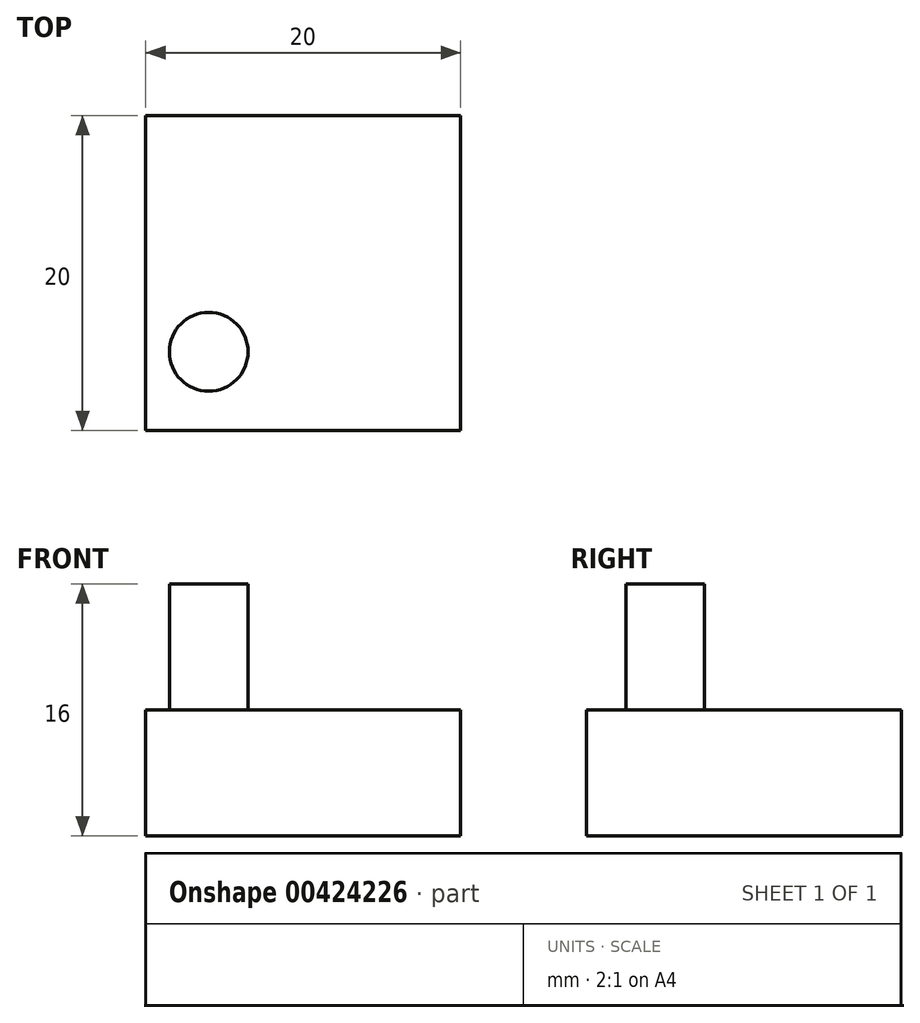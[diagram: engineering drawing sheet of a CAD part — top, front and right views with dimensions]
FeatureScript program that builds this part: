
annotation { "Feature Type Name" : "Feature", "Feature Type Description" : "" }
export const myFeature = defineFeature(function(context is Context, id is Id, definition is map)
    precondition{}
    {
        {
            var Q0;
            Q0=qCreatedBy(makeId("Top.planeOp"),FACE);
            var sketch = newSketch(context, id + "F0", { "sketchPlane" : qUnion([Q0])});
            skLineSegment(sketch, "E0.bottom", {"start": v(-10, 10) * mm, "end": v(10, 10) * mm});
            skLineSegment(sketch, "E0.top", {"start": v(-10, -10) * mm, "end": v(10, -10) * mm});
            skLineSegment(sketch, "E0.left", {"start": v(-10, 10) * mm, "end": v(-10, -10) * mm});
            skLineSegment(sketch, "E0.right", {"start": v(10, 10) * mm, "end": v(10, -10) * mm});
            skPoint(sketch, "E0.middle", {"position": v(0, 0) * mm});
            skSolve(sketch);
        }
        {
            var Q0;
            Q0=makeQuery(id+"F0.imprint","IMPRINT",FACE,{"disambiguationData":[TD([[makeQuery(id+"F0.imprint","IMPRINT",EDGE,{"derivedFrom":sQuery(id+"F0.wireOp",EDGE,"E0.bottom")}),-1.0]])]});
            var sketch = newSketch(context, id + "F1", { "sketchPlane" : qUnion([Q0])});
            skLineSegment(sketch, "E1", {"start": v(0, 0) * mm, "end": v(0, -5) * mm});
            skLineSegment(sketch, "E2", {"start": v(0, -5) * mm, "end": v(-6, -5) * mm});
            skCircle(sketch, "E3", {"center": v(-6, -5) * mm, "radius": 2.5 * mm});
            skSolve(sketch);
        }
        {
            var Q0;
            Q0 = qSketchRegion(id + "F1", true);
            extrude(context, id + "F2", {"entities" : qUnion([Q0]), "depth" : 8 * mm});
        }
        {
            var Q0;
            Q0=makeQuery(id+"F0.imprint","IMPRINT",FACE,{"disambiguationData":[TD([[makeQuery(id+"F0.imprint","IMPRINT",EDGE,{"derivedFrom":sQuery(id+"F0.wireOp",EDGE,"E0.bottom")}),-1.0]])]});
            extrude(context, id + "F3", {"entities" : qUnion([Q0]), "operationType" : NewBodyOperationType.ADD, "oppositeDirection" : true, "depth" : 8 * mm});
        }
    });
